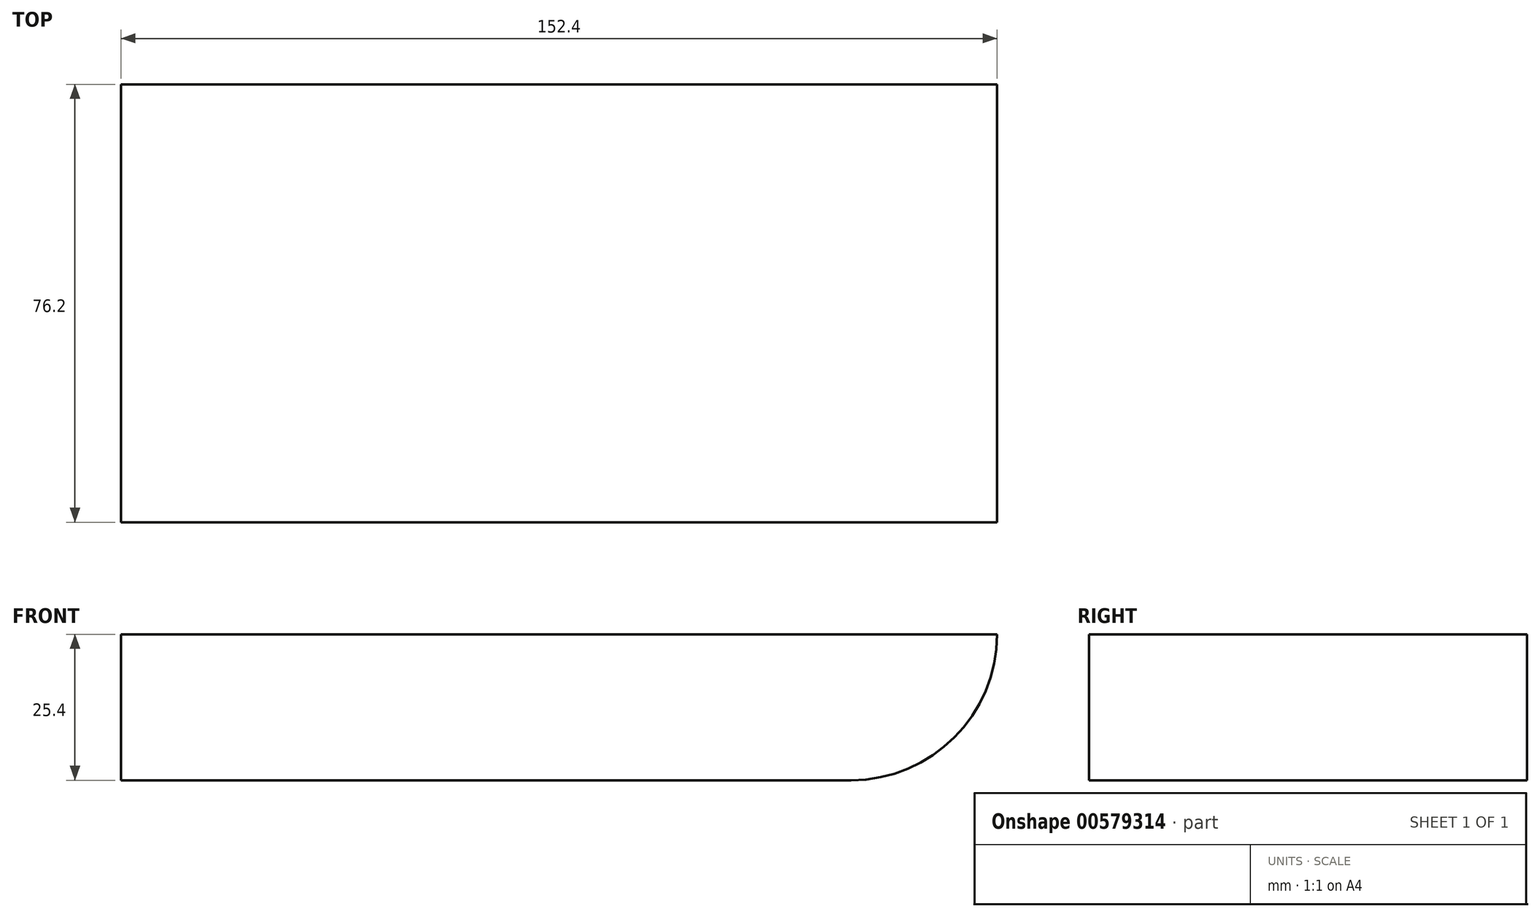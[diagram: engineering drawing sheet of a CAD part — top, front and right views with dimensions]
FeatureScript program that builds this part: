
annotation { "Feature Type Name" : "Feature", "Feature Type Description" : "" }
export const myFeature = defineFeature(function(context is Context, id is Id, definition is map)
    precondition{}
    {
        {
            var Q0;
            Q0=qCreatedBy(makeId("Front.planeOp"),FACE);
            var sketch = newSketch(context, id + "F0", { "sketchPlane" : qUnion([Q0])});
            skLineSegment(sketch, "E0.bottom", {"start": v(-67.2, 5.53) * mm, "end": v(59.8, 5.53) * mm});
            skLineSegment(sketch, "E0.top", {"start": v(-67.2, -19.87) * mm, "end": v(59.8, -19.87) * mm});
            skLineSegment(sketch, "E0.left", {"start": v(-67.2, 5.53) * mm, "end": v(-67.2, -19.87) * mm});
            skLineSegment(sketch, "E0.right", {"start": v(59.8, 5.53) * mm, "end": v(59.8, -19.87) * mm});
            skLineSegment(sketch, "E1", {"start": v(59.8, 5.53) * mm, "end": v(85.2, 5.53) * mm});
            skArc(sketch, "E2", {"start": v(59.8, -19.87) * mm, "mid": v(77.77, -12.43) * mm, "end": v(85.2, 5.53) * mm});
            skSolve(sketch);
        }
        {
            var Q0;
            Q0=makeQuery(id+"F0.imprint","IMPRINT",FACE,{"disambiguationData":[TD([[makeQuery(id+"F0.imprint","IMPRINT",EDGE,{"derivedFrom":sQuery(id+"F0.wireOp",EDGE,"E0.bottom")}),-1.0]])]});
            var Q1;
            Q1=makeQuery(id+"F0.imprint","IMPRINT",FACE,{"disambiguationData":[TD([[makeQuery(id+"F0.imprint","IMPRINT",EDGE,{"derivedFrom":sQuery(id+"F0.wireOp",EDGE,"E0.right")}),1.0]])]});
            extrude(context, id + "F1", {"entities" : qUnion([Q0, Q1]), "depth" : 76.2 * mm, "offsetDistance" : 25.4 * mm});
        }
    });
